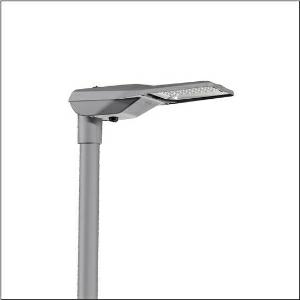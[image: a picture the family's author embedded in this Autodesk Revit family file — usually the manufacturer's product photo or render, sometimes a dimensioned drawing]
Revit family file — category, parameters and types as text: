
# Revit family: streetlight_sl_21_mini___st1_0a_5xe2d43t08jb_9874
name_source: partatom
category: Lighting Fixtures
units: mm (PartAtom-declared; Revit-internal decimal feet)

## family parameters
Cut with Voids When Loaded = No
Host = Face
Light Source = No
Part Type = Normal
Room Calculation Point = No
Round Connector Dimension = Use Diameter
Shared = No

## types (1)
- --- (1 x LED, 13500 lm, 88.6 W, 4000K)
    Apparent Load = 89 VA
    CIE Flux Codes = 40 73 97 100 100
    Color Rendering = 70
    Color Temperature = 4000K
    Default Elevation = 1800 mm
    Description = Streetlight SL 21 mini, mast luminaire, primary light control with lens, of PMMA, primary optical cover: cover, of toughened safety glass, transparent, light distribution: ST1.0a, light emission: direct distribution, primary light characteristic: asymmetric, installation type: side-entry, post-top, LED, High Power LED, rated luminous flux: 13.500lm, luminous efficacy: 152lm/W, light colour: 740, colour temperature: 4000K, control gear: D4i, control: overheat protection, constant luminous flux control, time-dependent luminous flux control, flexible luminous flux parameterisation, pre-setting: logarithmic dimming characteristic, mains connection: 220..240V, AC, 50/60Hz, start of lifetime: 89W, end of service life: 92W, reduction: 41W, luminaire housing, of diecast aluminium, powder-coated, Siteco® metallic grey (DB 702S), corrosivity category C5 mid according to DIN EN ISO 12944, please order mast flange separately, inclination adjustable: 0°, 5°, 10°, 15°, sealing non-destructively replaceable, multi-level sealing system, length: 628mm, width: 235mm, height: 110mm, mast flange for spigot size: 42mm (side-entry): 5XC10008XM4, 60/48mm (side-entry/post-top): 5XC10108XM2, 76/60mm (side-entry/post-top): 5XC10108XM1, mounting height: 4..8m, Smart Interface below and above, protection rating (complete): IP66, insulation class (complete): insulation class II (safety insulation), certification: CE, ENEC, ENEC+, VDE, impact resistance: IK10, permissible operating ambient temperature for outdoor applications: -40..+50°C, standard-compliant lighting for roads and squares, packaging unit: 1 piece

Light Distribution: ST1.0a
    Height = 110 mm
    Lamp = 1 x LED
    Lamp Light Flux = 13500 lm
    Lamp Power = 88.6 W
    Lamp count = 1
    Length = 625 mm
    Luminous efficacy = 152 lm/W
    Manufacturer = Siteco
    ModVariant = No
    Model = 5XE2D43T08JB
    Number of Poles = 1
    OnlyDefault = Yes
    Power Factor = 1
    Product Name = Streetlight SL 21 mini | ST1.0a
    Product group = mast luminaire | pylon top
    ProductGroupID = 6100
    Protection Class = Protection class II
    Protection Degree = IP 66
    RLX_Detail_Level = 1
    RLX_Emergency_Light_Flux = 0 lm
    RLX_Emergency_Type = 0
    RLX_Emergency_Type_DB = No
    RlxData = <blob elided: 26409 chars, md5=377e3692>
    Socket = socket
    Standby Power = 0 W
    System Light Flux = 13500 lm
    System Power = 89 W
    Type Comments = factory setting: luminous flux: 100 % | dim-lin: 254 | 915 mA
    Type Image = l_1003514.jpg
    URL = http://relux.com
    VarID = @adj_011757
    Voltage = 0 V
    Weight = 0.00 kg
    Width = 234 mm

## geometry (parser evidence)
native form markers: Blend x4, Sweep x8
no freeform markers — native parametric forms only
